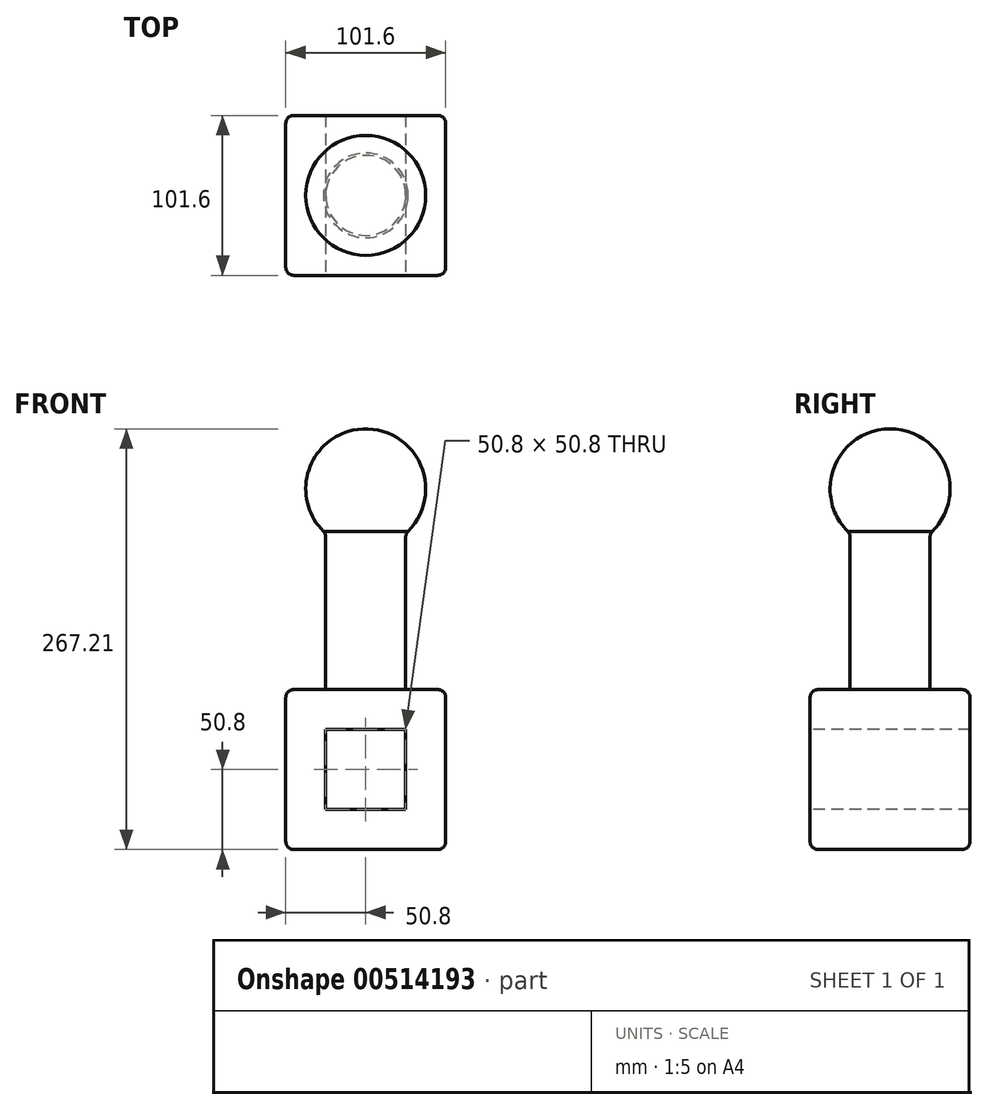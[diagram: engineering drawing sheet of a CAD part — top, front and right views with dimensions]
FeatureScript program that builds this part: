
annotation { "Feature Type Name" : "Feature", "Feature Type Description" : "" }
export const myFeature = defineFeature(function(context is Context, id is Id, definition is map)
    precondition{}
    {
        {
            var Q0;
            Q0=qCreatedBy(makeId("Top.planeOp"),FACE);
            var sketch = newSketch(context, id + "F0", { "sketchPlane" : qUnion([Q0])});
            skLineSegment(sketch, "E0.bottom", {"start": v(50.8, -50.8) * mm, "end": v(-50.8, -50.8) * mm});
            skLineSegment(sketch, "E0.top", {"start": v(50.8, 50.8) * mm, "end": v(-50.8, 50.8) * mm});
            skLineSegment(sketch, "E0.left", {"start": v(50.8, -50.8) * mm, "end": v(50.8, 50.8) * mm});
            skLineSegment(sketch, "E0.right", {"start": v(-50.8, -50.8) * mm, "end": v(-50.8, 50.8) * mm});
            skPoint(sketch, "E0.middle", {"position": v(0, 0) * mm});
            skSolve(sketch);
        }
        {
            var Q0;
            Q0 = qSketchRegion(id + "F0", true);
            extrude(context, id + "F1", {"entities" : qUnion([Q0]), "depth" : 101.6 * mm, "offsetDistance" : 25.4 * mm});
        }
        {
            var Q0;
            Q0=makeQuery(id+"F1.opExtrude","CAP_FACE",FACE,{"disambiguationData":[OSD([sQuery(id+"F0.wireOp",EDGE,"E0.bottom"),sQuery(id+"F0.wireOp",EDGE,"E0.top"),sQuery(id+"F0.wireOp",EDGE,"E0.left"),sQuery(id+"F0.wireOp",EDGE,"E0.right")])],"isStart":false});
            var sketch = newSketch(context, id + "F2", { "sketchPlane" : qUnion([Q0])});
            skCircle(sketch, "E1", {"center": v(0, 0) * mm, "radius": 25.4 * mm});
            skSolve(sketch);
        }
        {
            var Q0;
            Q0 = qSketchRegion(id + "F2", true);
            extrude(context, id + "F3", {"entities" : qUnion([Q0]), "operationType" : NewBodyOperationType.ADD, "depth" : 127.5 * mm, "offsetDistance" : 25.4 * mm});
        }
        {
            var Q0;
            Q0=makeQuery(id+"F3.opExtrude","CAP_FACE",FACE,{"disambiguationData":[OSD([sQuery(id+"F2.wireOp",EDGE,"E1")])],"isStart":false});
            var sketch = newSketch(context, id + "F4", { "sketchPlane" : qUnion([Q0])});
            skArc(sketch, "E2", {"start": v(0, -38.1) * mm, "mid": v(38.1, 0) * mm, "end": v(0, 38.1) * mm});
            skLineSegment(sketch, "E3", {"start": v(0, 38.1) * mm, "end": v(0, -38.1) * mm});
            skSolve(sketch);
        }
        {
            var Q0;
            {var subQ0=sQuery(id+"F4.wireOp",EDGE,"E2");Q0=makeQuery(id+"F4.imprint","IMPRINT",FACE,{"disambiguationData":[TD([[makeQuery(id+"F4.imprint","IMPRINT",EDGE,{"derivedFrom":subQ0}),1.0]])]});}
            var Q1;
            {var subQ0=sQuery(id+"F4.wireOp",EDGE,"E3");var subQ1=makeQuery(id+"F3.opExtrude","CAP_EDGE",EDGE,{"disambiguationData":[OSD([sQuery(id+"F2.wireOp",EDGE,"E1")])],"isStart":false});var subQ2=makeQuery(id+"F4.imprint","INTERSECT",VERTEX,{"disambiguationData":[OD(0.0)],"derivedFrom":[subQ1,subQ0]});Q1=makeQuery(id+"F4.imprint","IMPRINT",FACE,{"disambiguationData":[TD([[makeQuery(id+"F4.imprint","IMPRINT",EDGE,{"disambiguationData":[TD([[subQ2,-1.0]])],"derivedFrom":subQ0}),-1.0]])]});}
            var Q2;
            Q2=sQuery(id+"F4.wireOp",EDGE,"E3");
            revolve(context, id + "F5", {"operationType" : NewBodyOperationType.ADD, "entities" : qUnion([Q0, Q1]), "axis" : qUnion([Q2]), "revolveType" : RevolveType.FULL});
        }
        {
            var Q0;
            Q0=makeQuery(id+"F1.opExtrude","SWEPT_FACE",FACE,{"disambiguationData":[OSD([sQuery(id+"F0.wireOp",EDGE,"E0.bottom")])]});
            var sketch = newSketch(context, id + "F6", { "sketchPlane" : qUnion([Q0])});
            skLineSegment(sketch, "E4.bottom", {"start": v(25.4, 25.4) * mm, "end": v(-25.4, 25.4) * mm});
            skLineSegment(sketch, "E4.top", {"start": v(25.4, 76.2) * mm, "end": v(-25.4, 76.2) * mm});
            skLineSegment(sketch, "E4.left", {"start": v(25.4, 25.4) * mm, "end": v(25.4, 76.2) * mm});
            skLineSegment(sketch, "E4.right", {"start": v(-25.4, 25.4) * mm, "end": v(-25.4, 76.2) * mm});
            skPoint(sketch, "E4.middle", {"position": v(0, 50.8) * mm});
            skSolve(sketch);
        }
        {
            var Q0;
            Q0=makeQuery(id+"F6.imprint","IMPRINT",FACE,{"disambiguationData":[TD([[makeQuery(id+"F6.imprint","IMPRINT",EDGE,{"derivedFrom":sQuery(id+"F6.wireOp",EDGE,"E4.bottom")}),-1.0]])]});
            extrude(context, id + "F7", {"entities" : qUnion([Q0]), "operationType" : NewBodyOperationType.REMOVE, "oppositeDirection" : true, "depth" : 101.6 * mm, "offsetDistance" : 25.4 * mm});
        }
        {
            var Q0;
            Q0=makeQuery(id+"F1.opExtrude","CAP_EDGE",EDGE,{"disambiguationData":[OSD([sQuery(id+"F0.wireOp",EDGE,"E0.bottom")])],"isStart":false});
            var Q1;
            Q1=makeQuery(id+"F1.opExtrude","CAP_EDGE",EDGE,{"disambiguationData":[OSD([sQuery(id+"F0.wireOp",EDGE,"E0.right")])],"isStart":false});
            var Q2;
            Q2=makeQuery(id+"F1.opExtrude","CAP_EDGE",EDGE,{"disambiguationData":[OSD([sQuery(id+"F0.wireOp",EDGE,"E0.left")])],"isStart":false});
            var Q3;
            Q3=makeQuery(id+"F1.opExtrude","CAP_EDGE",EDGE,{"disambiguationData":[OSD([sQuery(id+"F0.wireOp",EDGE,"E0.top")])],"isStart":false});
            var Q4;
            Q4=makeQuery(id+"F1.opExtrude","SWEPT_EDGE",EDGE,{"disambiguationData":[OSD([sQuery(id+"F0.wireOp",EDGE,"E0.bottom"),sQuery(id+"F0.wireOp",EDGE,"E0.left")])]});
            var Q5;
            Q5=makeQuery(id+"F1.opExtrude","SWEPT_EDGE",EDGE,{"disambiguationData":[OSD([sQuery(id+"F0.wireOp",EDGE,"E0.top"),sQuery(id+"F0.wireOp",EDGE,"E0.left")])]});
            var Q6;
            Q6=makeQuery(id+"F1.opExtrude","CAP_EDGE",EDGE,{"disambiguationData":[OSD([sQuery(id+"F0.wireOp",EDGE,"E0.left")])],"isStart":true});
            var Q7;
            Q7=makeQuery(id+"F1.opExtrude","CAP_EDGE",EDGE,{"disambiguationData":[OSD([sQuery(id+"F0.wireOp",EDGE,"E0.bottom")])],"isStart":true});
            var Q8;
            Q8=makeQuery(id+"F1.opExtrude","SWEPT_EDGE",EDGE,{"disambiguationData":[OSD([sQuery(id+"F0.wireOp",EDGE,"E0.bottom"),sQuery(id+"F0.wireOp",EDGE,"E0.right")])]});
            var Q9;
            Q9=makeQuery(id+"F1.opExtrude","SWEPT_FACE",FACE,{"disambiguationData":[OSD([sQuery(id+"F0.wireOp",EDGE,"E0.right")])]});
            var Q10;
            Q10=makeQuery(id+"F1.opExtrude","SWEPT_EDGE",EDGE,{"disambiguationData":[OSD([sQuery(id+"F0.wireOp",EDGE,"E0.top"),sQuery(id+"F0.wireOp",EDGE,"E0.right")])]});
            var Q11;
            Q11=makeQuery(id+"F1.opExtrude","CAP_EDGE",EDGE,{"disambiguationData":[OSD([sQuery(id+"F0.wireOp",EDGE,"E0.top")])],"isStart":true});
            var Q12;
            Q12=makeQuery(id+"F5.boolean.opBoolean","INTERSECT",EDGE,{"derivedFrom":[makeQuery(id+"F3.opExtrude","SWEPT_FACE",FACE,{"disambiguationData":[OSD([sQuery(id+"F2.wireOp",EDGE,"E1")])]}),makeQuery(id+"F5.opRevolve","SWEPT_FACE",FACE,{"disambiguationData":[OSD([sQuery(id+"F4.wireOp",EDGE,"E2")])]})]});
            var Q13;
            Q13=makeQuery(id+"F3.opExtrude","CAP_EDGE",EDGE,{"disambiguationData":[OSD([sQuery(id+"F2.wireOp",EDGE,"E1")])],"isStart":true});
            fillet(context, id + "F8", {"entities" : qUnion([Q0, Q1, Q2, Q3, Q4, Q5, Q6, Q7, Q8, Q9, Q10, Q11, Q12, Q13]), "radius" : 5.08 * mm, "tangentPropagation" : true, "allowEdgeOverflow" : false});
        }
    });
